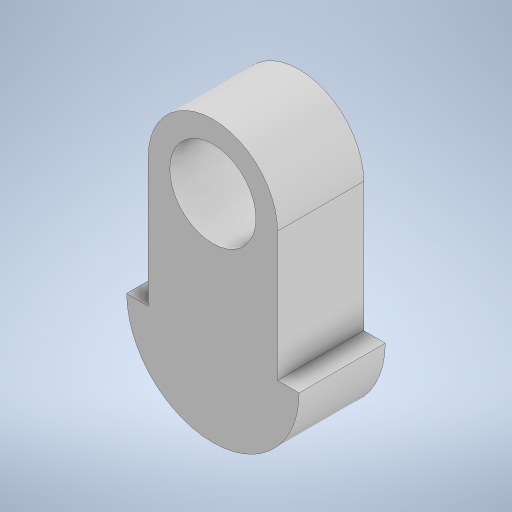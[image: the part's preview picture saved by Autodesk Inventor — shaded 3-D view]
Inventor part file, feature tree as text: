
AUTODESK INVENTOR PART (.ipt)
format: ipt  version: 2024 (Build 280153000, 153)  size: 236,544 bytes
history: native  units: mm
features: extrude x1, sketch x1
ambient origin geometry x8: Origin, YZ Plane, XZ Plane, XY Plane, X Axis, Y Axis, Z Axis, Center Point
bodies: Solid1 (feature_tree)
feature tree (2):
  extrude  "Extrusion1"  Depth=8.0mm
  sketch  "Sketch1"  dims[d0=16.0mm d1=2.0mm d2=8.0mm d3=2.0mm d9=20.0mm d10=8.0mm d11=0.0mm]
